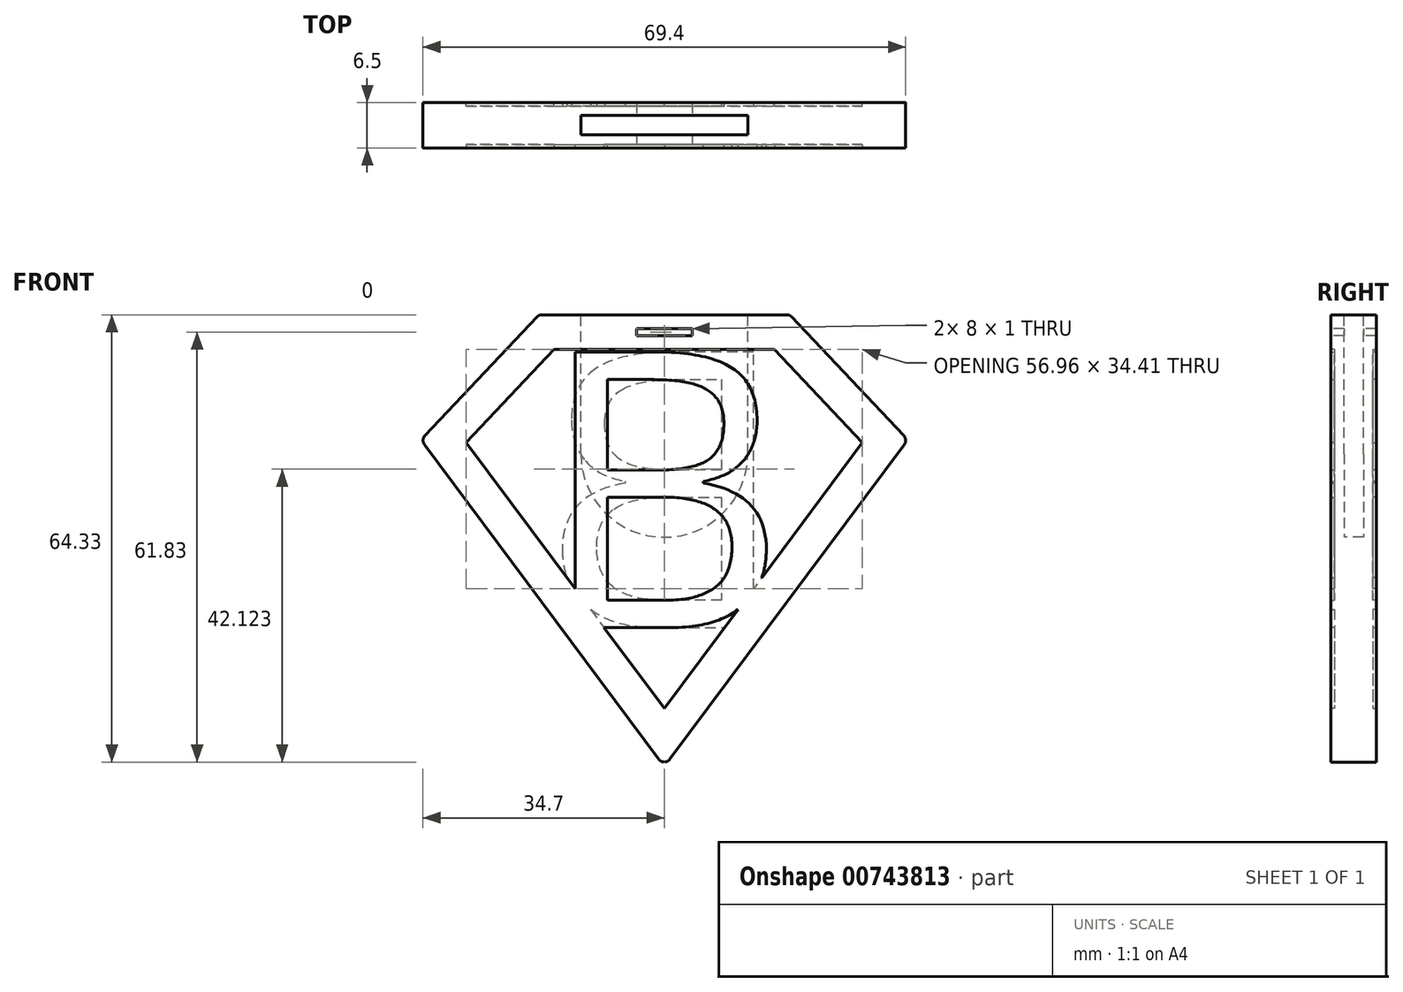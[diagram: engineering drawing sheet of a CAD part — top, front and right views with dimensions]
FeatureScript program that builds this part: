
annotation { "Feature Type Name" : "Feature", "Feature Type Description" : "" }
export const myFeature = defineFeature(function(context is Context, id is Id, definition is map)
    precondition{}
    {
        {
            var Q0;
            Q0=qCreatedBy(makeId("Front.planeOp"),FACE);
            var sketch = newSketch(context, id + "F0", { "sketchPlane" : qUnion([Q0])});
            skLineSegment(sketch, "E0", {"start": v(0, 18) * mm, "end": v(18, 18) * mm});
            skLineSegment(sketch, "E1", {"start": v(18, 18) * mm, "end": v(35, 0) * mm});
            skLineSegment(sketch, "E2", {"start": v(35, 0) * mm, "end": v(0, -47) * mm});
            skLineSegment(sketch, "E3", {"start": v(0, 18) * mm, "end": v(0, -47) * mm, "construction": true});
            skLineSegment(sketch, "E4.MirrorCS", {"start": v(-35, 0) * mm, "end": v(0, -47) * mm});
            skLineSegment(sketch, "E5.MirrorCS", {"start": v(-18, 18) * mm, "end": v(-35, 0) * mm});
            skLineSegment(sketch, "E6.MirrorCS", {"start": v(0, 18) * mm, "end": v(-18, 18) * mm});
            skSolve(sketch);
        }
        {
            var Q0;
            Q0=qSketchRegion(id+"F0",true);
            extrude(context, id + "F1", {"entities" : qUnion([Q0]), "endBound" : BoundingType.SYMMETRIC, "depth" : 6.5 * mm, "offsetDistance" : 25 * mm});
        }
        {
            var Q0;
            Q0=makeQuery(id+"F1.opExtrude","CAP_FACE",FACE,{"disambiguationData":[OSD([sQuery(id+"F0.wireOp",EDGE,"E0"),sQuery(id+"F0.wireOp",EDGE,"E1"),sQuery(id+"F0.wireOp",EDGE,"E2"),sQuery(id+"F0.wireOp",EDGE,"E4.MirrorCS"),sQuery(id+"F0.wireOp",EDGE,"E5.MirrorCS"),sQuery(id+"F0.wireOp",EDGE,"E6.MirrorCS")])],"isStart":false});
            var sketch = newSketch(context, id + "F2", { "sketchPlane" : qUnion([Q0])});
            skLineSegment(sketch, "E7.0", {"start": v(-15.84, 13) * mm, "end": v(15.84, 13) * mm});
            skLineSegment(sketch, "E8.0", {"start": v(-15.84, 13) * mm, "end": v(-28.48, -0.38) * mm});
            skLineSegment(sketch, "E9.0", {"start": v(-28.48, -0.38) * mm, "end": v(0, -38.63) * mm});
            skLineSegment(sketch, "E10.0", {"start": v(28.48, -0.38) * mm, "end": v(0, -38.63) * mm});
            skLineSegment(sketch, "E11.0", {"start": v(15.84, 13) * mm, "end": v(28.48, -0.38) * mm});
            skSolve(sketch);
        }
        {
            var Q0;
            Q0=qSketchRegion(id+"F2",true);
            extrude(context, id + "F3", {"entities" : qUnion([Q0]), "operationType" : NewBodyOperationType.REMOVE, "oppositeDirection" : true, "depth" : 0.5 * mm, "offsetDistance" : 25 * mm});
        }
        {
            var Q0;
            Q0=makeQuery(id+"F1.opExtrude","CAP_FACE",FACE,{"disambiguationData":[OSD([sQuery(id+"F0.wireOp",EDGE,"E0"),sQuery(id+"F0.wireOp",EDGE,"E1"),sQuery(id+"F0.wireOp",EDGE,"E2"),sQuery(id+"F0.wireOp",EDGE,"E4.MirrorCS"),sQuery(id+"F0.wireOp",EDGE,"E5.MirrorCS"),sQuery(id+"F0.wireOp",EDGE,"E6.MirrorCS")])],"isStart":true});
            var sketch = newSketch(context, id + "F4", { "sketchPlane" : qUnion([Q0])});
            skLineSegment(sketch, "E12.0", {"start": v(15.84, 13) * mm, "end": v(-15.84, 13) * mm});
            skLineSegment(sketch, "E13.0", {"start": v(15.84, 13) * mm, "end": v(28.48, -0.38) * mm});
            skLineSegment(sketch, "E14.0", {"start": v(28.48, -0.38) * mm, "end": v(0, -38.63) * mm});
            skLineSegment(sketch, "E15.0", {"start": v(-28.48, -0.38) * mm, "end": v(0, -38.63) * mm});
            skLineSegment(sketch, "E15.1", {"start": v(-15.84, 13) * mm, "end": v(-28.48, -0.38) * mm});
            skSolve(sketch);
        }
        {
            var Q0;
            Q0=qSketchRegion(id+"F4",true);
            extrude(context, id + "F5", {"entities" : qUnion([Q0]), "operationType" : NewBodyOperationType.REMOVE, "oppositeDirection" : true, "depth" : 0.5 * mm, "offsetDistance" : 25 * mm});
        }
        {
            var Q0;
            Q0=makeQuery(id+"F3.boolean.opBoolean","COPY",FACE,{"derivedFrom":makeQuery(id+"F3.opExtrude","CAP_FACE",FACE,{"disambiguationData":[OSD([sQuery(id+"F2.wireOp",EDGE,"E7.0"),sQuery(id+"F2.wireOp",EDGE,"E8.0"),sQuery(id+"F2.wireOp",EDGE,"E9.0"),sQuery(id+"F2.wireOp",EDGE,"E10.0"),sQuery(id+"F2.wireOp",EDGE,"E11.0")])],"isStart":false})});
            var sketch = newSketch(context, id + "F6", { "sketchPlane" : qUnion([Q0])});
            skText(sketch, "E16", { "text": "B", "fontName": "OpenSans-Regular.ttf"});
            const initialGuessF6  = {"E16": [-0.01827, -0.027, 1, 0, 0.04]};
            skSetInitialGuess(sketch, initialGuessF6);
            skSolve(sketch);
        }
        {
            var Q0;
            Q0=qSketchRegion(id+"F6",true);
            extrude(context, id + "F7", {"entities" : qUnion([Q0]), "operationType" : NewBodyOperationType.ADD, "depth" : 0.5 * mm, "offsetDistance" : 25 * mm});
        }
        {
            var Q0;
            Q0=makeQuery(id+"F5.boolean.opBoolean","COPY",FACE,{"derivedFrom":makeQuery(id+"F5.opExtrude","CAP_FACE",FACE,{"disambiguationData":[OSD([sQuery(id+"F4.wireOp",EDGE,"E12.0"),sQuery(id+"F4.wireOp",EDGE,"E13.0"),sQuery(id+"F4.wireOp",EDGE,"E14.0"),sQuery(id+"F4.wireOp",EDGE,"E15.0"),sQuery(id+"F4.wireOp",EDGE,"E15.1")])],"isStart":false})});
            var sketch = newSketch(context, id + "F8", { "sketchPlane" : qUnion([Q0])});
            skText(sketch, "E17", { "text": "B", "fontName": "OpenSans-Regular.ttf"});
            const initialGuessF8  = {"E17": [-0.01827, -0.027, 1, 0, 0.04]};
            skSetInitialGuess(sketch, initialGuessF8);
            skSolve(sketch);
        }
        {
            var Q0;
            Q0=qSketchRegion(id+"F8",true);
            extrude(context, id + "F9", {"entities" : qUnion([Q0]), "operationType" : NewBodyOperationType.ADD, "depth" : 0.5 * mm, "offsetDistance" : 25 * mm});
        }
        {
            var Q0;
            Q0=makeQuery(id+"F1.opExtrude","SWEPT_FACE",FACE,{"disambiguationData":[OSD([sQuery(id+"F0.wireOp",EDGE,"E0"),sQuery(id+"F0.wireOp",EDGE,"E6.MirrorCS")])]});
            var sketch = newSketch(context, id + "F10", { "sketchPlane" : qUnion([Q0])});
            skLineSegment(sketch, "E18.bottom", {"start": v(-12, 1.4) * mm, "end": v(12, 1.4) * mm});
            skLineSegment(sketch, "E18.top", {"start": v(-12, -1.4) * mm, "end": v(12, -1.4) * mm});
            skLineSegment(sketch, "E18.left", {"start": v(-12, 1.4) * mm, "end": v(-12, -1.4) * mm});
            skLineSegment(sketch, "E18.right", {"start": v(12, 1.4) * mm, "end": v(12, -1.4) * mm});
            skSolve(sketch);
        }
        {
            var Q0;
            Q0=qSketchRegion(id+"F10",true);
            extrude(context, id + "F11", {"entities" : qUnion([Q0]), "operationType" : NewBodyOperationType.REMOVE, "oppositeDirection" : true, "depth" : 20 * mm, "offsetDistance" : 25 * mm});
        }
        {
            var Q0;
            Q0=qCreatedBy(makeId("Front.planeOp"),FACE);
            var sketch = newSketch(context, id + "F12", { "sketchPlane" : qUnion([Q0])});
            skLineSegment(sketch, "E19.0", {"start": v(-12, -2) * mm, "end": v(12, -2) * mm});
            skArc(sketch, "E20", {"start": v(-12, -2) * mm, "mid": v(0, -14) * mm, "end": v(12, -2) * mm});
            skSolve(sketch);
        }
        {
            var Q0;
            Q0=qSketchRegion(id+"F12",true);
            extrude(context, id + "F13", {"entities" : qUnion([Q0]), "operationType" : NewBodyOperationType.REMOVE, "endBound" : BoundingType.SYMMETRIC, "oppositeDirection" : true, "depth" : 2.8 * mm, "offsetDistance" : 25 * mm});
        }
        {
            var Q0;
            Q0=makeQuery(id+"F1.opExtrude","CAP_FACE",FACE,{"disambiguationData":[OSD([sQuery(id+"F0.wireOp",EDGE,"E0"),sQuery(id+"F0.wireOp",EDGE,"E1"),sQuery(id+"F0.wireOp",EDGE,"E2"),sQuery(id+"F0.wireOp",EDGE,"E4.MirrorCS"),sQuery(id+"F0.wireOp",EDGE,"E5.MirrorCS"),sQuery(id+"F0.wireOp",EDGE,"E6.MirrorCS")])],"isStart":false});
            var sketch = newSketch(context, id + "F14", { "sketchPlane" : qUnion([Q0])});
            skLineSegment(sketch, "E21.bottom", {"start": v(-4, 16) * mm, "end": v(4, 16) * mm});
            skLineSegment(sketch, "E21.top", {"start": v(-4, 15) * mm, "end": v(4, 15) * mm});
            skLineSegment(sketch, "E21.left", {"start": v(-4, 16) * mm, "end": v(-4, 15) * mm});
            skLineSegment(sketch, "E21.right", {"start": v(4, 16) * mm, "end": v(4, 15) * mm});
            skSolve(sketch);
        }
        {
            var Q0;
            Q0=qSketchRegion(id+"F14",true);
            extrude(context, id + "F15", {"entities" : qUnion([Q0]), "operationType" : NewBodyOperationType.REMOVE, "oppositeDirection" : true, "depth" : 25 * mm, "offsetDistance" : 25 * mm});
        }
        {
            var Q0;
            Q0=makeQuery(id+"F1.opExtrude","SWEPT_EDGE",EDGE,{"disambiguationData":[OSD([sQuery(id+"F0.wireOp",EDGE,"E2"),sQuery(id+"F0.wireOp",EDGE,"E4.MirrorCS")])]});
            var Q1;
            Q1=makeQuery(id+"F1.opExtrude","SWEPT_EDGE",EDGE,{"disambiguationData":[OSD([sQuery(id+"F0.wireOp",EDGE,"E1"),sQuery(id+"F0.wireOp",EDGE,"E2")])]});
            var Q2;
            Q2=makeQuery(id+"F1.opExtrude","SWEPT_EDGE",EDGE,{"disambiguationData":[OSD([sQuery(id+"F0.wireOp",EDGE,"E4.MirrorCS"),sQuery(id+"F0.wireOp",EDGE,"E5.MirrorCS")])]});
            var Q3;
            Q3=makeQuery(id+"F1.opExtrude","SWEPT_EDGE",EDGE,{"disambiguationData":[OSD([sQuery(id+"F0.wireOp",EDGE,"E5.MirrorCS"),sQuery(id+"F0.wireOp",EDGE,"E6.MirrorCS")])]});
            var Q4;
            Q4=makeQuery(id+"F1.opExtrude","SWEPT_EDGE",EDGE,{"disambiguationData":[OSD([sQuery(id+"F0.wireOp",EDGE,"E0"),sQuery(id+"F0.wireOp",EDGE,"E1")])]});
            fillet(context, id + "F16", {"entities" : qUnion([Q0, Q1, Q2, Q3, Q4]), "radius" : 1 * mm, "tangentPropagation" : true, "allowEdgeOverflow" : false});
        }
    });
